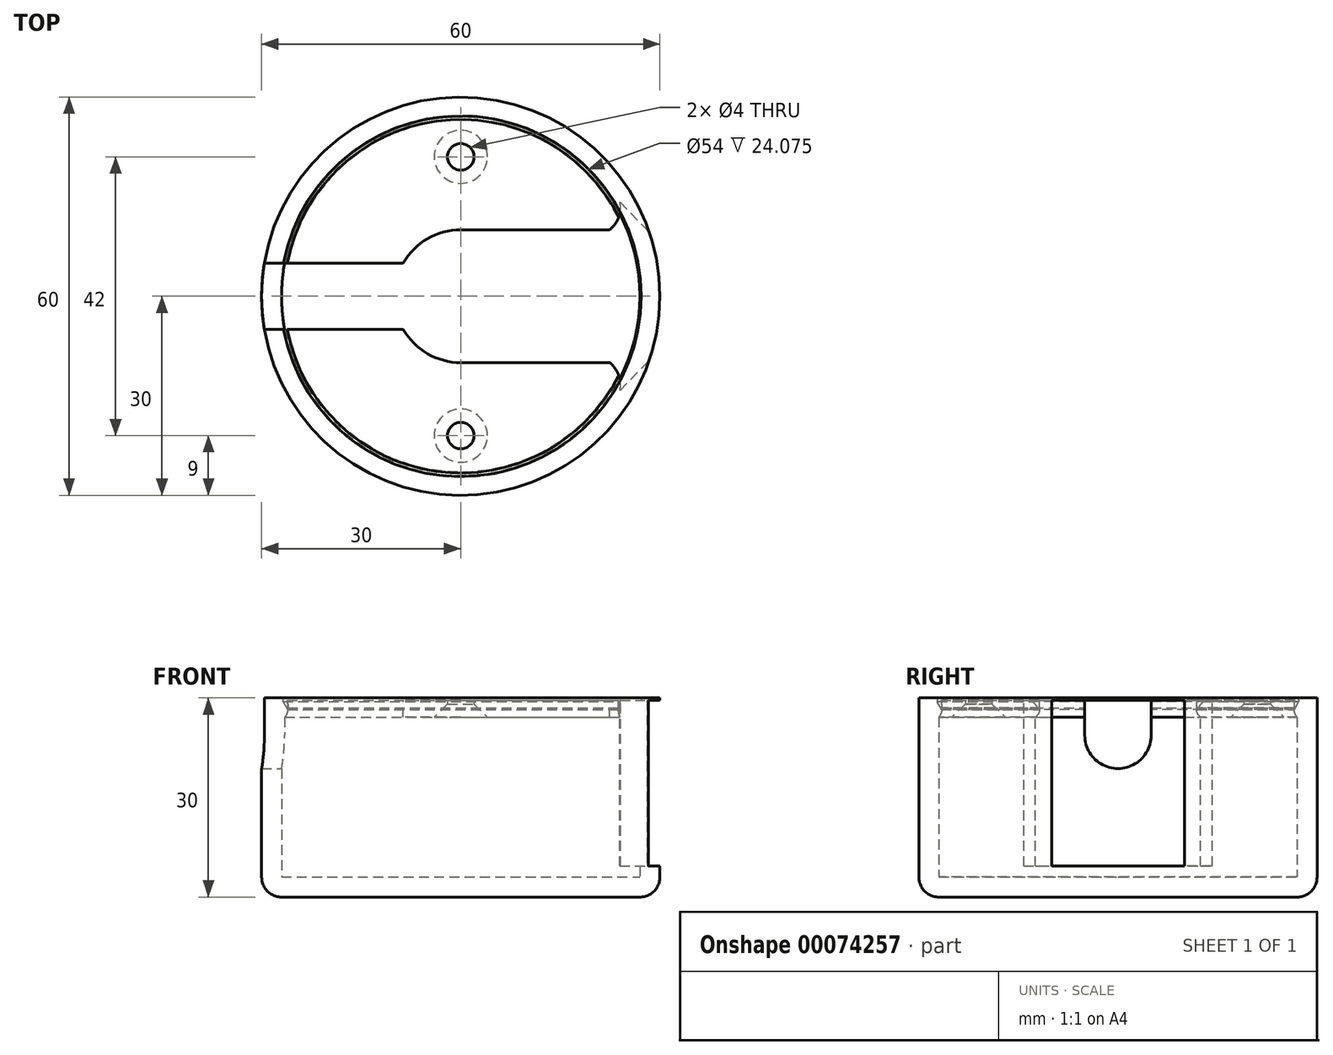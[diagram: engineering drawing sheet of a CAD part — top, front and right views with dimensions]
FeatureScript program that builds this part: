
annotation { "Feature Type Name" : "Feature", "Feature Type Description" : "" }
export const myFeature = defineFeature(function(context is Context, id is Id, definition is map)
    precondition{}
    {
        {
            var Q0;
            Q0=qCreatedBy(makeId("Front.planeOp"),FACE);
            var sketch = newSketch(context, id + "F0", { "sketchPlane" : qUnion([Q0])});
            skLineSegment(sketch, "E0", {"start": v(0, 0) * mm, "end": v(27, 0) * mm});
            skLineSegment(sketch, "E1", {"start": v(30, 3) * mm, "end": v(30, 30) * mm});
            skLineSegment(sketch, "E2", {"start": v(30, 30) * mm, "end": v(27, 30) * mm});
            skLineSegment(sketch, "E3", {"start": v(27, 3) * mm, "end": v(0, 3) * mm});
            skLineSegment(sketch, "E4.trimOffspring", {"start": v(27, 27.08) * mm, "end": v(27, 3) * mm});
            skPoint(sketch, "E5.visualSharp", {"position": v(30, 0) * mm});
            skArc(sketch, "E5.filletArc", {"start": v(27, 0) * mm, "mid": v(29.12, 0.88) * mm, "end": v(30, 3) * mm});
            skArc(sketch, "E6", {"start": v(27, 29.66) * mm, "mid": v(26.53, 28.37) * mm, "end": v(27, 27.08) * mm});
            skLineSegment(sketch, "E7", {"start": v(27, 30) * mm, "end": v(27, 29.66) * mm});
            skLineSegment(sketch, "E8", {"start": v(27, 29.66) * mm, "end": v(0, 29.66) * mm});
            skLineSegment(sketch, "E9", {"start": v(27, 27.08) * mm, "end": v(0, 27.08) * mm});
            skLineSegment(sketch, "E10", {"start": v(0, 29.66) * mm, "end": v(0, 27.08) * mm});
            skLineSegment(sketch, "E11", {"start": v(0, 3) * mm, "end": v(0, 0) * mm});
            skLineSegment(sketch, "E12", {"start": v(0, 0) * mm, "end": v(0, 41.43) * mm, "construction": true});
            skLineSegment(sketch, "E13", {"start": v(0, 0) * mm, "end": v(14.42, -9.7) * mm, "construction": true});
            skSolve(sketch);
        }
        {
            var Q0;
            Q0=makeQuery(id+"F0.imprint","IMPRINT",FACE,{"disambiguationData":[TD([[makeQuery(id+"F0.imprint","IMPRINT",EDGE,{"derivedFrom":sQuery(id+"F0.wireOp",EDGE,"E0")}),1.0]])]});
            var Q1;
            Q1=sQuery(id+"F0.wireOp",EDGE,"E12");
            revolve(context, id + "F1", {"entities" : qUnion([Q0]), "axis" : qUnion([Q1]), "revolveType" : RevolveType.FULL});
        }
        {
            var Q0;
            Q0=makeQuery(id+"F0.imprint","IMPRINT",FACE,{"disambiguationData":[TD([[makeQuery(id+"F0.imprint","IMPRINT",EDGE,{"derivedFrom":sQuery(id+"F0.wireOp",EDGE,"E6")}),-1.0]])]});
            var Q1;
            Q1=sQuery(id+"F0.wireOp",EDGE,"E12");
            revolve(context, id + "F2", {"operationType" : NewBodyOperationType.ADD, "entities" : qUnion([Q0]), "axis" : qUnion([Q1]), "revolveType" : RevolveType.FULL});
        }
        {
            var Q0;
            Q0=makeQuery(id+"F0.imprint","IMPRINT",FACE,{"disambiguationData":[TD([[makeQuery(id+"F0.imprint","IMPRINT",EDGE,{"derivedFrom":sQuery(id+"F0.wireOp",EDGE,"E6")}),-1.0]])]});
            var Q1;
            Q1=sQuery(id+"F0.wireOp",EDGE,"E12");
            revolve(context, id + "F3", {"entities" : qUnion([Q0]), "axis" : qUnion([Q1]), "revolveType" : RevolveType.FULL});
        }
        {
            var Q0;
            Q0=qCreatedBy(makeId("Front.planeOp"),FACE);
            var sketch = newSketch(context, id + "F4", { "sketchPlane" : qUnion([Q0])});
            skArc(sketch, "E14", {"start": v(27.07, 30.66) * mm, "mid": v(26.6, 29.5) * mm, "end": v(26.57, 28.24) * mm});
            skLineSegment(sketch, "E15", {"start": v(27.07, 30.66) * mm, "end": v(27.24, 29.45) * mm});
            skLineSegment(sketch, "E16", {"start": v(27.24, 29.45) * mm, "end": v(26.57, 28.24) * mm});
            skSolve(sketch);
        }
        {
            var Q0;
            Q0 = qSketchRegion(id + "F4", true);
            var Q1;
            Q1=sQuery(id+"F0.wireOp",EDGE,"E12");
            revolve(context, id + "F5", {"operationType" : NewBodyOperationType.REMOVE, "entities" : qUnion([Q0]), "axis" : qUnion([Q1]), "revolveType" : RevolveType.FULL, "oppositeDirection" : true});
        }
        {
            var Q0;
            Q0=makeQuery(id+"F3.opRevolve","SWEPT_FACE",FACE,{"disambiguationData":[OSD([sQuery(id+"F0.wireOp",EDGE,"E8")])]});
            var sketch = newSketch(context, id + "F6", { "sketchPlane" : qUnion([Q0])});
            skLineSegment(sketch, "E17", {"start": v(39.6, 0) * mm, "end": v(-41.62, 0) * mm, "construction": true});
            skCircle(sketch, "E18", {"center": v(0, 0) * mm, "radius": 10 * mm});
            skLineSegment(sketch, "E19", {"start": v(0, 10) * mm, "end": v(43.64, 10) * mm});
            skLineSegment(sketch, "E20", {"start": v(0, -10) * mm, "end": v(44.3, -10) * mm});
            skLineSegment(sketch, "E21", {"start": v(43.64, 10) * mm, "end": v(44.3, -10) * mm});
            skSolve(sketch);
        }
        {
            var Q0;
            Q0 = qSketchRegion(id + "F6", true);
            extrude(context, id + "F7", {"entities" : qUnion([Q0]), "operationType" : NewBodyOperationType.REMOVE, "oppositeDirection" : true, "depth" : 25 * mm});
        }
        {
            var Q0;
            Q0=makeQuery(id+"F3.opRevolve","SWEPT_FACE",FACE,{"disambiguationData":[OSD([sQuery(id+"F0.wireOp",EDGE,"E8")])]});
            var sketch = newSketch(context, id + "F8", { "sketchPlane" : qUnion([Q0])});
            skArc(sketch, "E22", {"start": v(18.74, 9.14) * mm, "mid": v(22.72, 10.25) * mm, "end": v(23.99, 14.18) * mm});
            skLineSegment(sketch, "E23", {"start": v(23.99, 14.18) * mm, "end": v(30.4, 7.61) * mm});
            skLineSegment(sketch, "E24", {"start": v(30.4, 7.61) * mm, "end": v(19.85, 7.04) * mm});
            skLineSegment(sketch, "E25", {"start": v(19.85, 7.04) * mm, "end": v(18.74, 9.14) * mm});
            skArc(sketch, "E26.MirrorCS", {"start": v(18.74, -9.14) * mm, "mid": v(22.72, -10.25) * mm, "end": v(23.99, -14.18) * mm});
            skLineSegment(sketch, "E27.MirrorCS", {"start": v(30.4, -7.61) * mm, "end": v(19.85, -7.04) * mm});
            skLineSegment(sketch, "E28.MirrorCS", {"start": v(19.85, -7.04) * mm, "end": v(18.74, -9.14) * mm});
            skLineSegment(sketch, "E29.MirrorCS", {"start": v(23.99, -14.18) * mm, "end": v(30.4, -7.61) * mm});
            skSolve(sketch);
        }
        {
            var Q0;
            Q0 = qSketchRegion(id + "F8", true);
            extrude(context, id + "F9", {"entities" : qUnion([Q0]), "operationType" : NewBodyOperationType.REMOVE, "oppositeDirection" : true, "depth" : 25 * mm});
        }
        {
            var Q0;
            Q0=makeQuery(id+"F3.opRevolve","SWEPT_FACE",FACE,{"disambiguationData":[OSD([sQuery(id+"F0.wireOp",EDGE,"E9")])]});
            var sketch = newSketch(context, id + "F10", { "sketchPlane" : qUnion([Q0])});
            skCircle(sketch, "E30", {"center": v(0, 21) * mm, "radius": 2 * mm});
            skCircle(sketch, "E31.MirrorC", {"center": v(0, -21) * mm, "radius": 2 * mm});
            skSolve(sketch);
        }
        {
            var Q0;
            Q0=sQuery(id+"F10.wireOp",VERTEX,"E30.center");
            var Q1;
            Q1=sQuery(id+"F10.wireOp",VERTEX,"E31.MirrorC.center");
            var Q2;
            Q2=makeQuery(id+"F3.opRevolve","SWEPT_BODY",BODY,{"disambiguationData":[OSD([sQuery(id+"F0.wireOp",EDGE,"E6"),sQuery(id+"F0.wireOp",EDGE,"E8"),sQuery(id+"F0.wireOp",EDGE,"E9"),sQuery(id+"F0.wireOp",EDGE,"E10")])]});
            hole(context, id + "F11", {"style" : HoleStyle.C_SINK, "holeDiameter" : 4 * mm, "cSinkDiameter" : 8 * mm, "endStyle" : HoleEndStyle.THROUGH, "locations" : qUnion([Q0, Q1]), "scope" : qUnion([Q2]), "cSinkAngle" : 90 * degree});
        }
        {
            var Q0;
            Q0=qCreatedBy(makeId("Right.planeOp"),FACE);
            var sketch = newSketch(context, id + "F12", { "sketchPlane" : qUnion([Q0])});
            skLineSegment(sketch, "E32", {"start": v(5, 32.2) * mm, "end": v(5, 24.34) * mm});
            skLineSegment(sketch, "E33", {"start": v(-5, 24.34) * mm, "end": v(-5, 32.5) * mm});
            skArc(sketch, "E34", {"start": v(-5, 24.34) * mm, "mid": v(0, 19.34) * mm, "end": v(5, 24.34) * mm});
            skLineSegment(sketch, "E35", {"start": v(5, 32.2) * mm, "end": v(-5, 32.5) * mm});
            skSolve(sketch);
        }
        {
            var Q0;
            Q0 = qSketchRegion(id + "F12", true);
            extrude(context, id + "F13", {"entities" : qUnion([Q0]), "operationType" : NewBodyOperationType.REMOVE, "endBound" : BoundingType.THROUGH_ALL, "oppositeDirection" : true, "depth" : 25 * mm});
        }
    });
